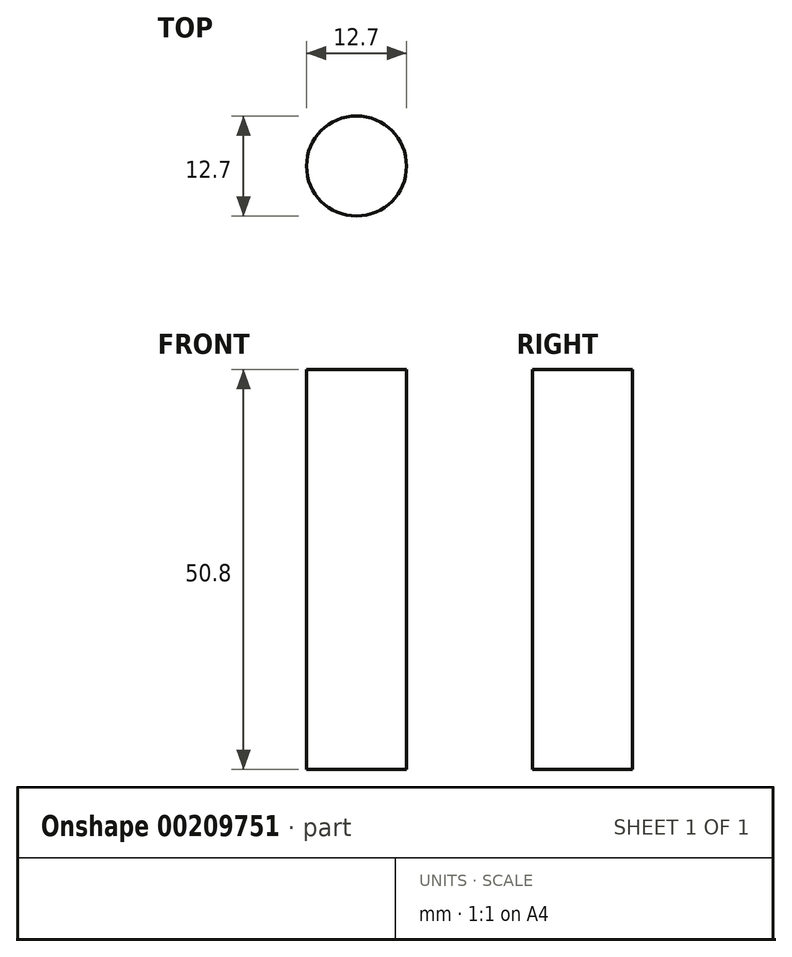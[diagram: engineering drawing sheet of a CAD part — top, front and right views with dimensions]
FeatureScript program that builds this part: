
annotation { "Feature Type Name" : "Feature", "Feature Type Description" : "" }
export const myFeature = defineFeature(function(context is Context, id is Id, definition is map)
    precondition{}
    {
        {
            var Q0;
            Q0=qCreatedBy(makeId("Front.planeOp"),FACE);
            var sketch = newSketch(context, id + "F0", { "sketchPlane" : qUnion([Q0])});
            skLineSegment(sketch, "E0.bottom", {"start": v(0, 0) * mm, "end": v(6.35, 0) * mm});
            skLineSegment(sketch, "E0.top", {"start": v(0, 50.8) * mm, "end": v(6.35, 50.8) * mm});
            skLineSegment(sketch, "E0.left", {"start": v(0, 0) * mm, "end": v(0, 50.8) * mm});
            skLineSegment(sketch, "E0.right", {"start": v(6.35, 0) * mm, "end": v(6.35, 50.8) * mm});
            skSolve(sketch);
        }
        {
            var Q0;
            Q0=makeQuery(id+"F0.imprint","IMPRINT",FACE,{"disambiguationData":[TD([[makeQuery(id+"F0.imprint","IMPRINT",EDGE,{"derivedFrom":sQuery(id+"F0.wireOp",EDGE,"E0.bottom")}),1.0]])]});
            var Q1;
            Q1=sQuery(id+"F0.wireOp",EDGE,"E0.left");
            revolve(context, id + "F1", {"entities" : qUnion([Q0]), "axis" : qUnion([Q1]), "revolveType" : RevolveType.FULL});
        }
    });
